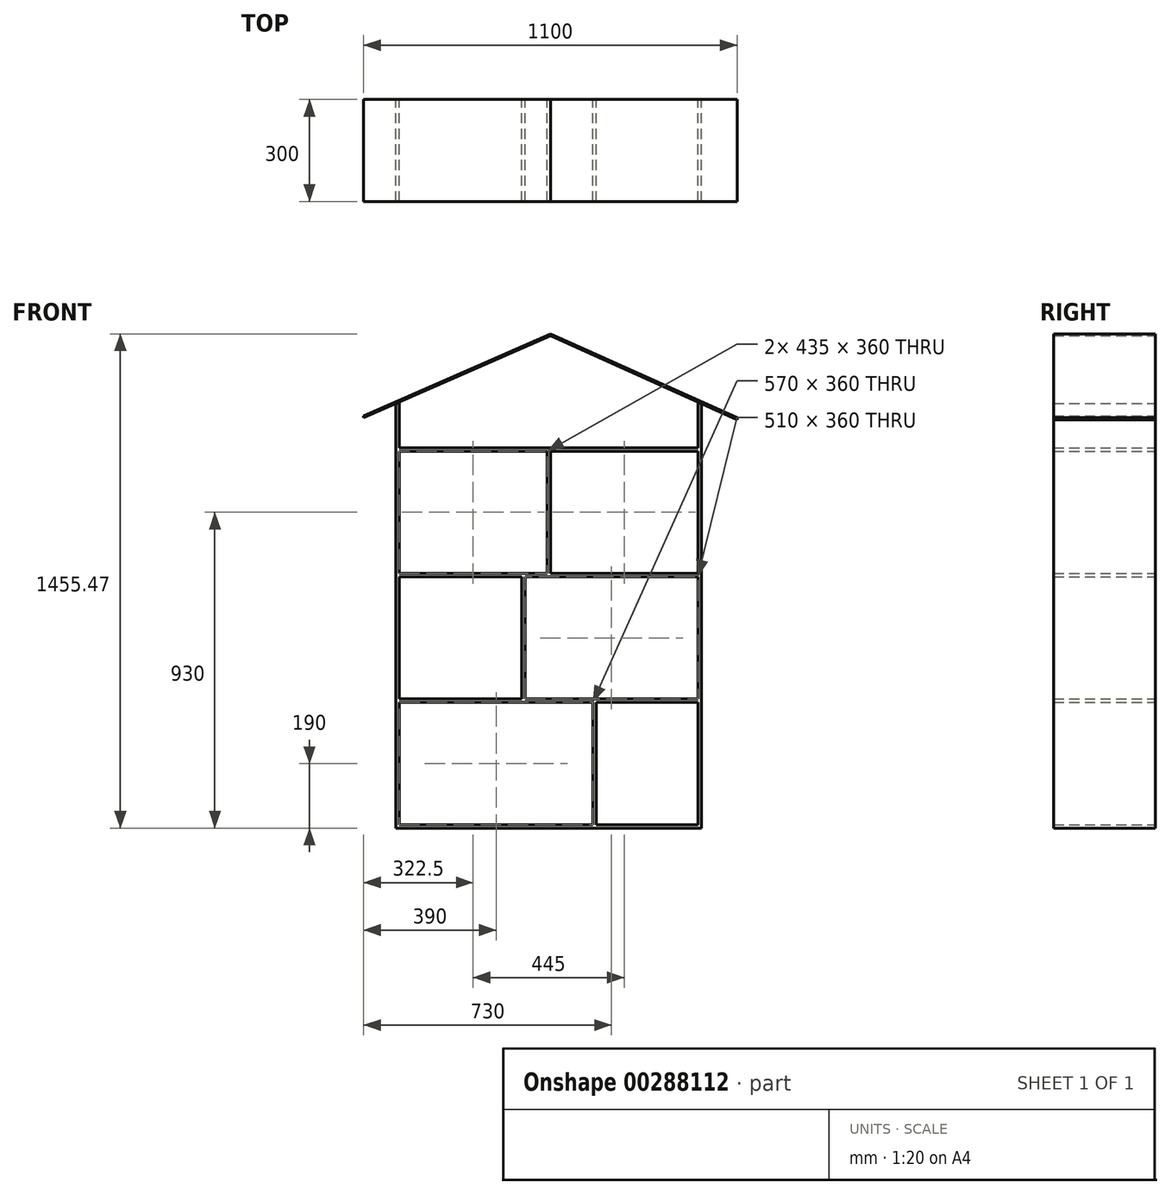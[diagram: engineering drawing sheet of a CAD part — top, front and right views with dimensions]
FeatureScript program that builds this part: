
annotation { "Feature Type Name" : "Feature", "Feature Type Description" : "" }
export const myFeature = defineFeature(function(context is Context, id is Id, definition is map)
    precondition{}
    {
        {
            var Q0;
            Q0=qCreatedBy(makeId("Front.planeOp"),FACE);
            var sketch = newSketch(context, id + "F0", { "sketchPlane" : qUnion([Q0])});
            skLineSegment(sketch, "E0", {"start": v(10, 0) * mm, "end": v(580, 0) * mm});
            skLineSegment(sketch, "E1", {"start": v(0, -10) * mm, "end": v(0, 1240) * mm});
            skLineSegment(sketch, "E2", {"start": v(900, -10) * mm, "end": v(900, 1240) * mm});
            skLineSegment(sketch, "E3.0", {"start": v(890, 0) * mm, "end": v(890, 360) * mm});
            skLineSegment(sketch, "E4.0", {"start": v(0, -10) * mm, "end": v(900, -10) * mm});
            skLineSegment(sketch, "E5.0", {"start": v(10, 0) * mm, "end": v(10, 360) * mm});
            skLineSegment(sketch, "E6.0", {"start": v(10, 360) * mm, "end": v(580, 360) * mm});
            skLineSegment(sketch, "E7.0", {"start": v(10, 370) * mm, "end": v(370, 370) * mm});
            skLineSegment(sketch, "E8.0", {"start": v(10, 730) * mm, "end": v(370, 730) * mm});
            skLineSegment(sketch, "E9.0", {"start": v(10, 740) * mm, "end": v(445, 740) * mm});
            skLineSegment(sketch, "E10.0", {"start": v(10, 1100) * mm, "end": v(445, 1100) * mm});
            skLineSegment(sketch, "E11.0", {"start": v(10, 1110) * mm, "end": v(890, 1110) * mm});
            skLineSegment(sketch, "E12.0", {"start": v(590, 0) * mm, "end": v(590, 360) * mm});
            skLineSegment(sketch, "E13.0", {"start": v(370, 370) * mm, "end": v(370, 730) * mm});
            skLineSegment(sketch, "E14.trimOffspring", {"start": v(890, 1110) * mm, "end": v(890, 1240) * mm});
            skLineSegment(sketch, "E15.trimOffspring", {"start": v(10, 1110) * mm, "end": v(10, 1240) * mm});
            skLineSegment(sketch, "E16.trimOffspring", {"start": v(10, 740) * mm, "end": v(10, 1100) * mm});
            skLineSegment(sketch, "E17.trimOffspring", {"start": v(10, 370) * mm, "end": v(10, 730) * mm});
            skLineSegment(sketch, "E18.0", {"start": v(580, 0) * mm, "end": v(580, 360) * mm});
            skLineSegment(sketch, "E19.0", {"start": v(380, 370) * mm, "end": v(380, 730) * mm});
            skLineSegment(sketch, "E20.trimOffspring", {"start": v(380, 730) * mm, "end": v(890, 730) * mm});
            skLineSegment(sketch, "E21.trimOffspring", {"start": v(380, 370) * mm, "end": v(890, 370) * mm});
            skLineSegment(sketch, "E22.trimOffspring", {"start": v(590, 360) * mm, "end": v(890, 360) * mm});
            skLineSegment(sketch, "E23.trimOffspring", {"start": v(890, 370) * mm, "end": v(890, 730) * mm});
            skLineSegment(sketch, "E24.trimOffspring", {"start": v(590, 0) * mm, "end": v(890, 0) * mm});
            skLineSegment(sketch, "E25.0", {"start": v(445, 740) * mm, "end": v(445, 1100) * mm});
            skLineSegment(sketch, "E26.0", {"start": v(455, 740) * mm, "end": v(455, 1100) * mm});
            skLineSegment(sketch, "E27.trimOffspring", {"start": v(890, 740) * mm, "end": v(890, 1100) * mm});
            skLineSegment(sketch, "E28.trimOffspring", {"start": v(455, 740) * mm, "end": v(890, 740) * mm});
            skLineSegment(sketch, "E29.trimOffspring", {"start": v(455, 1100) * mm, "end": v(890, 1100) * mm});
            skLineSegment(sketch, "E30", {"start": v(-95, 1198.24) * mm, "end": v(455, 1440) * mm});
            skLineSegment(sketch, "E31", {"start": v(455, 1440) * mm, "end": v(1005, 1192.8) * mm});
            skLineSegment(sketch, "E32", {"start": v(455, 1100) * mm, "end": v(455, 1561.57) * mm, "construction": true});
            skLineSegment(sketch, "E33.0", {"start": v(-95, 1203.7) * mm, "end": v(455.02, 1445.47) * mm});
            skLineSegment(sketch, "E34.0", {"start": v(455.02, 1445.47) * mm, "end": v(1005, 1198.3) * mm});
            skLineSegment(sketch, "E35", {"start": v(-95, 1198.24) * mm, "end": v(-95, 1203.7) * mm});
            skLineSegment(sketch, "E36", {"start": v(1005, 1192.8) * mm, "end": v(1005, 1198.3) * mm});
            skPoint(sketch, "E37.orphan", {"position": v(1005, 1192.8) * mm});
            skLineSegment(sketch, "E38", {"start": v(0, 1240) * mm, "end": v(10, 1240) * mm});
            skLineSegment(sketch, "E39", {"start": v(900, 1240) * mm, "end": v(890, 1240) * mm});
            skSolve(sketch);
        }
        {
            var Q0;
            Q0=makeQuery(id+"F0.imprint","IMPRINT",FACE,{"disambiguationData":[TD([[makeQuery(id+"F0.imprint","IMPRINT",EDGE,{"derivedFrom":sQuery(id+"F0.wireOp",EDGE,"E33.0")}),-1.0]])]});
            var Q1;
            Q1=makeQuery(id+"F0.imprint","IMPRINT",FACE,{"disambiguationData":[TD([[makeQuery(id+"F0.imprint","IMPRINT",EDGE,{"derivedFrom":sQuery(id+"F0.wireOp",EDGE,"E0")}),-1.0]])]});
            extrude(context, id + "F1", {"entities" : qUnion([Q0, Q1]), "depth" : 300 * mm});
        }
    });
